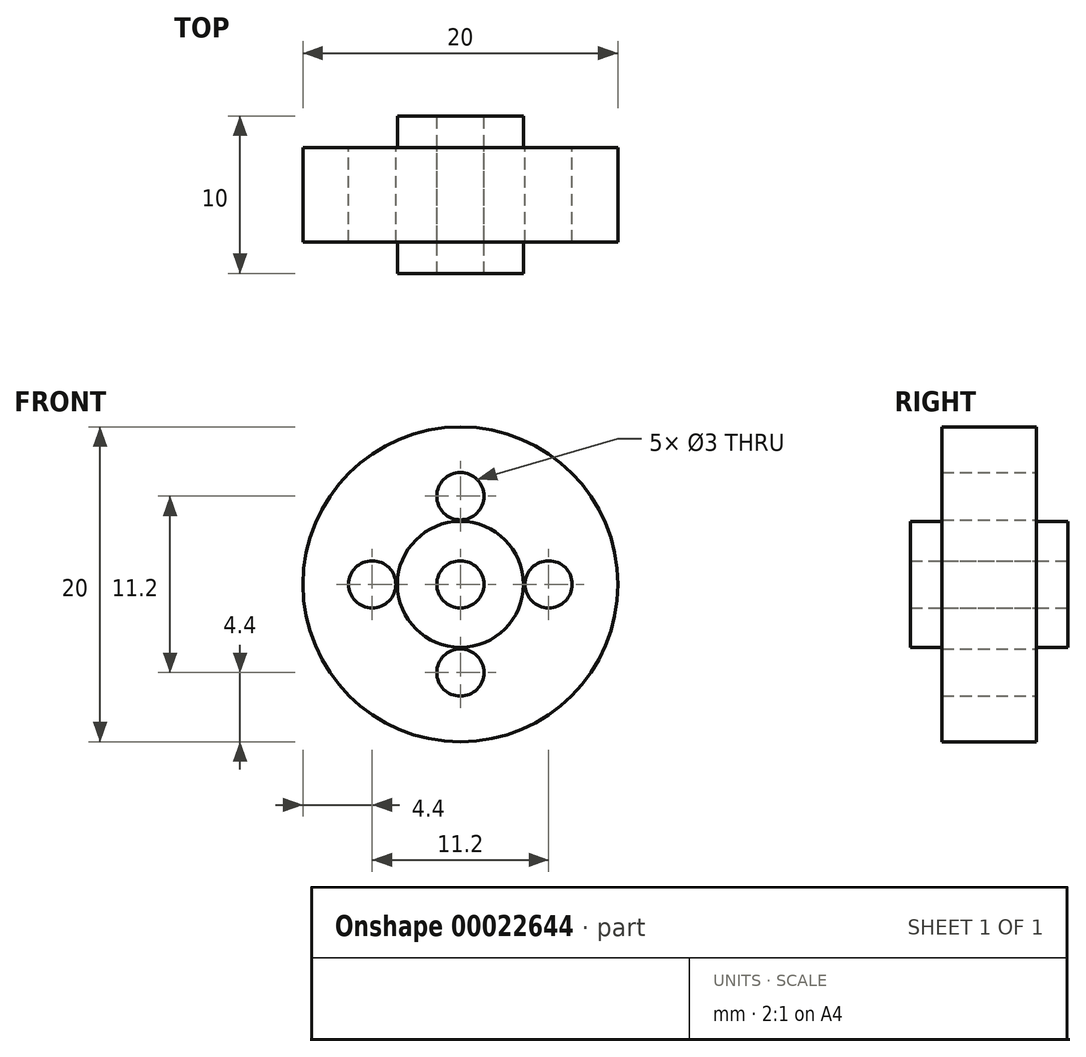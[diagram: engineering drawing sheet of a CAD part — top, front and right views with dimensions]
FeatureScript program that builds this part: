
annotation { "Feature Type Name" : "Feature", "Feature Type Description" : "" }
export const myFeature = defineFeature(function(context is Context, id is Id, definition is map)
    precondition{}
    {
        {
            var Q0;
            Q0=qCreatedBy(makeId("Front.planeOp"),FACE);
            var sketch = newSketch(context, id + "F0", { "sketchPlane" : qUnion([Q0])});
            skCircle(sketch, "E0", {"center": v(0, 0) * mm, "radius": 10 * mm});
            skCircle(sketch, "E1", {"center": v(0, 0) * mm, "radius": 4 * mm});
            skCircle(sketch, "E2", {"center": v(0, 0) * mm, "radius": 1.5 * mm});
            skCircle(sketch, "E3", {"center": v(0, 5.6) * mm, "radius": 1.5 * mm});
            skCircle(sketch, "E4.1.0", {"center": v(-5.6, 0) * mm, "radius": 1.5 * mm});
            skCircle(sketch, "E4.2.0", {"center": v(0, -5.6) * mm, "radius": 1.5 * mm});
            skCircle(sketch, "E4.3.0", {"center": v(5.6, 0) * mm, "radius": 1.5 * mm});
            skSolve(sketch);
        }
        {
            var Q0;
            Q0 = qSketchRegion(id + "F0", true);
            extrude(context, id + "F1", {"entities" : qUnion([Q0]), "endBound" : BoundingType.SYMMETRIC, "depth" : 6 * mm});
        }
        {
            var Q0;
            Q0=makeQuery(id+"F0.imprint","IMPRINT",FACE,{"disambiguationData":[TD([[makeQuery(id+"F0.imprint","IMPRINT",EDGE,{"derivedFrom":sQuery(id+"F0.wireOp",EDGE,"E1")}),1.0]])]});
            extrude(context, id + "F2", {"entities" : qUnion([Q0]), "operationType" : NewBodyOperationType.ADD, "endBound" : BoundingType.SYMMETRIC, "depth" : 10 * mm});
        }
    });
